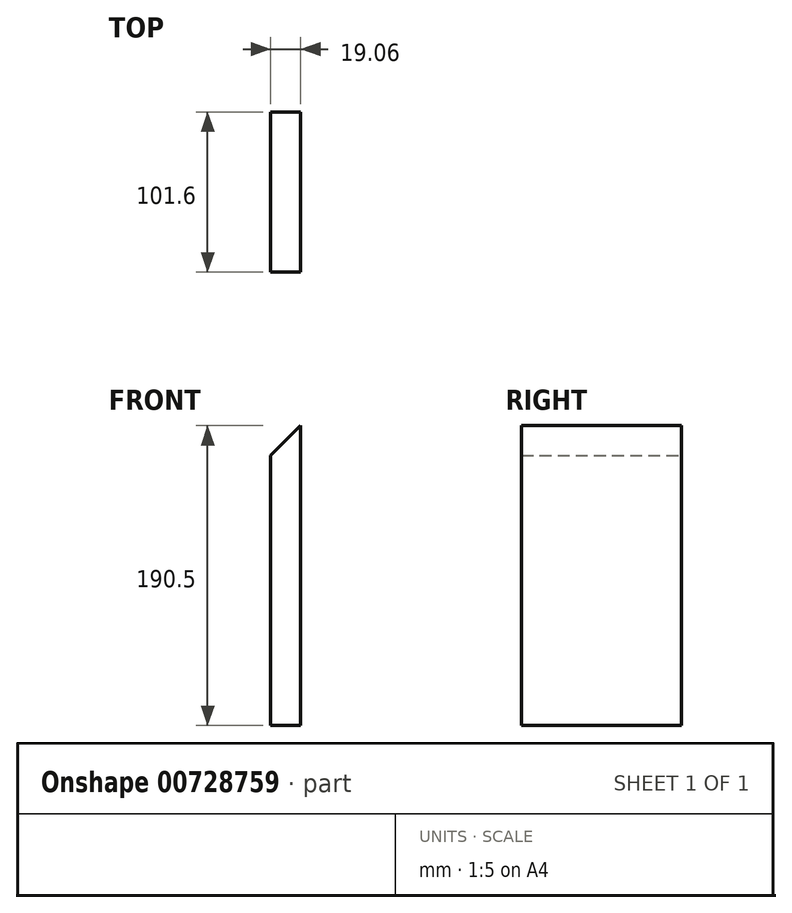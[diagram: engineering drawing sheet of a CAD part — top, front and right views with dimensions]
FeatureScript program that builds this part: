
annotation { "Feature Type Name" : "Feature", "Feature Type Description" : "" }
export const myFeature = defineFeature(function(context is Context, id is Id, definition is map)
    precondition{}
    {
        {
            var Q0;
            Q0=qCreatedBy(makeId("Top.planeOp"),FACE);
            var sketch = newSketch(context, id + "F0", { "sketchPlane" : qUnion([Q0])});
            skLineSegment(sketch, "E0.bottom", {"start": v(9.52, -50.8) * mm, "end": v(-9.53, -50.8) * mm});
            skLineSegment(sketch, "E0.top", {"start": v(9.53, 50.8) * mm, "end": v(-9.52, 50.8) * mm});
            skLineSegment(sketch, "E0.left", {"start": v(9.52, -50.8) * mm, "end": v(9.53, 50.8) * mm});
            skLineSegment(sketch, "E0.right", {"start": v(-9.53, -50.8) * mm, "end": v(-9.52, 50.8) * mm});
            skPoint(sketch, "E0.middle", {"position": v(0, 0) * mm});
            skSolve(sketch);
        }
        {
            var Q0;
            Q0 = qSketchRegion(id + "F0", true);
            extrude(context, id + "F1", {"entities" : qUnion([Q0]), "depth" : 190.5 * mm, "offsetDistance" : 25.4 * mm});
        }
        {
            var Q0;
            Q0=makeQuery(id+"F1.opExtrude","CAP_EDGE",EDGE,{"disambiguationData":[OSD([sQuery(id+"F0.wireOp",EDGE,"E0.right")])],"isStart":false});
            chamfer(context, id + "F2", {"entities" : qUnion([Q0]), "width" : 19.05 * mm, "tangentPropagation" : true});
        }
    });
